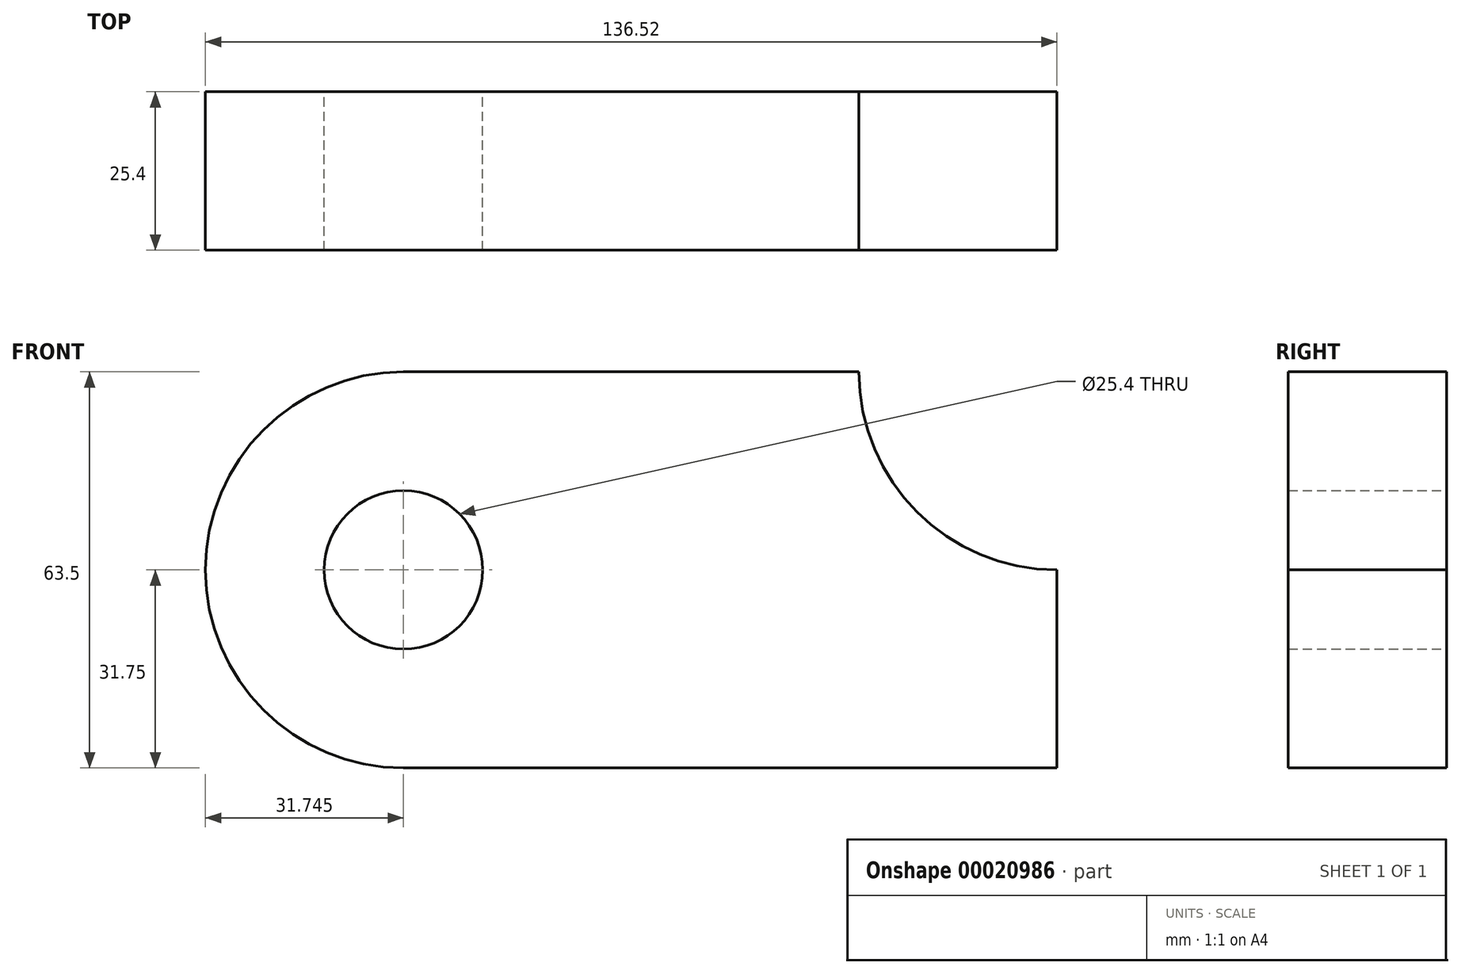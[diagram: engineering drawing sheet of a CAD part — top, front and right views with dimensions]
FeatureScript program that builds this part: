
annotation { "Feature Type Name" : "Feature", "Feature Type Description" : "" }
export const myFeature = defineFeature(function(context is Context, id is Id, definition is map)
    precondition{}
    {
        {
            var Q0;
            Q0=qCreatedBy(makeId("Front.planeOp"),FACE);
            var sketch = newSketch(context, id + "F0", { "sketchPlane" : qUnion([Q0])});
            skLineSegment(sketch, "E0.bottom", {"start": v(0, 0) * mm, "end": v(-104.78, 0) * mm});
            skLineSegment(sketch, "E0.top", {"start": v(0, 63.5) * mm, "end": v(-104.78, 63.5) * mm});
            skLineSegment(sketch, "E0.left", {"start": v(0, 0) * mm, "end": v(0, 63.5) * mm});
            skLineSegment(sketch, "E0.right", {"start": v(-104.78, 0) * mm, "end": v(-104.78, 63.5) * mm});
            skCircle(sketch, "E1", {"center": v(-104.78, 31.75) * mm, "radius": 31.75 * mm});
            skCircle(sketch, "E2", {"center": v(0, 63.5) * mm, "radius": 31.75 * mm});
            skCircle(sketch, "E3", {"center": v(-104.78, 31.75) * mm, "radius": 12.7 * mm});
            skSolve(sketch);
        }
        {
            var Q0;
            {var subQ8=sQuery(id+"F0.wireOp",EDGE,"E0.bottom");Q0=makeQuery(id+"F0.imprint","IMPRINT",FACE,{"disambiguationData":[TD([[makeQuery(id+"F0.imprint","IMPRINT",EDGE,{"derivedFrom":subQ8}),-1.0]])]});}
            var Q1;
            {var subQ0=sQuery(id+"F0.wireOp",EDGE,"E3");var subQ1=sQuery(id+"F0.wireOp",EDGE,"E0.right");var subQ3=makeQuery(id+"F0.imprint","INTERSECT",VERTEX,{"disambiguationData":[OD(0.0)],"derivedFrom":[subQ1,subQ0]});Q1=makeQuery(id+"F0.imprint","IMPRINT",FACE,{"disambiguationData":[TD([[makeQuery(id+"F0.imprint","IMPRINT",EDGE,{"disambiguationData":[TD([[subQ3,1.0]])],"derivedFrom":subQ0}),-1.0]])]});}
            var Q2;
            {var subQ0=sQuery(id+"F0.wireOp",EDGE,"E3");var subQ1=sQuery(id+"F0.wireOp",EDGE,"E0.right");var subQ3=makeQuery(id+"F0.imprint","INTERSECT",VERTEX,{"disambiguationData":[OD(0.0)],"derivedFrom":[subQ1,subQ0]});Q2=makeQuery(id+"F0.imprint","IMPRINT",FACE,{"disambiguationData":[TD([[makeQuery(id+"F0.imprint","IMPRINT",EDGE,{"disambiguationData":[TD([[subQ3,-1.0]])],"derivedFrom":subQ0}),-1.0]])]});}
            extrude(context, id + "F1", {"entities" : qUnion([Q0, Q1, Q2]), "depth" : 25.4 * mm});
        }
    });
